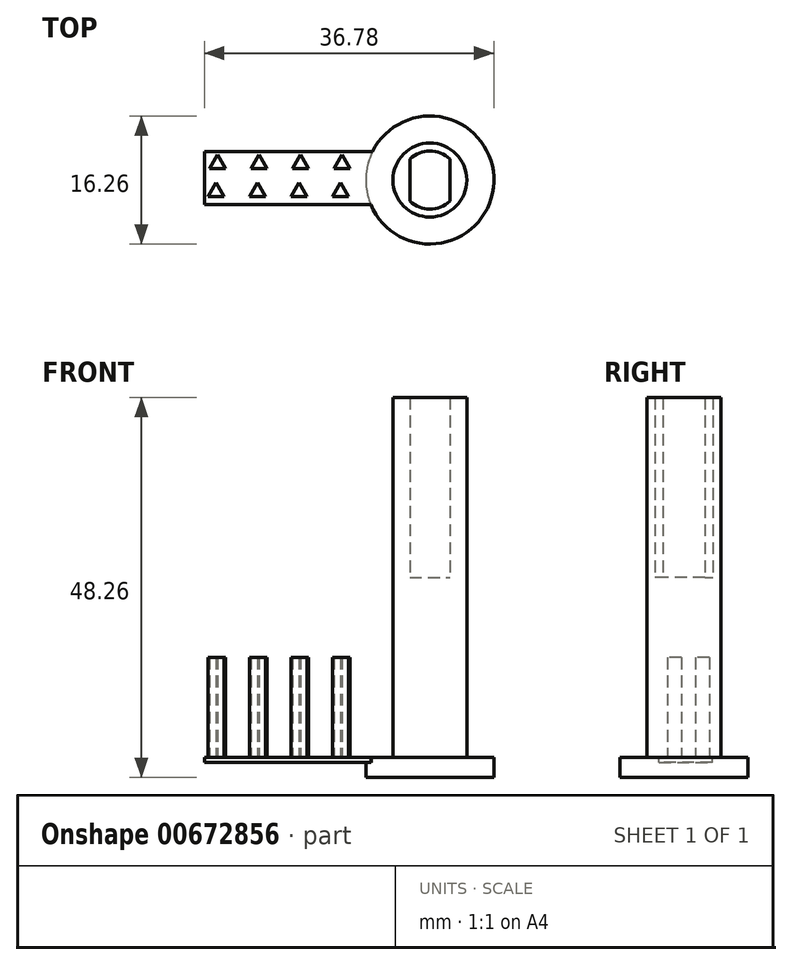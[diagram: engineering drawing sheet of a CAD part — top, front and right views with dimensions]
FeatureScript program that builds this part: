
annotation { "Feature Type Name" : "Feature", "Feature Type Description" : "" }
export const myFeature = defineFeature(function(context is Context, id is Id, definition is map)
    precondition{}
    {
        {
            var Q0;
            Q0=qCreatedBy(makeId("Top.planeOp"),FACE);
            var sketch = newSketch(context, id + "F0", { "sketchPlane" : qUnion([Q0])});
            skCircle(sketch, "E0", {"center": v(0, 0) * mm, "radius": 4.7 * mm});
            skCircle(sketch, "E1", {"center": v(0, 0) * mm, "radius": 3.68 * mm});
            skLineSegment(sketch, "E2", {"start": v(0, 0) * mm, "end": v(-2.54, 0) * mm});
            skLineSegment(sketch, "E3", {"start": v(0, 0) * mm, "end": v(2.54, 0) * mm});
            skLineSegment(sketch, "E4.bottom", {"start": v(2.54, 2.67) * mm, "end": v(3.77, 2.67) * mm});
            skLineSegment(sketch, "E4.top", {"start": v(2.54, -2.8) * mm, "end": v(3.77, -2.8) * mm});
            skLineSegment(sketch, "E4.left", {"start": v(2.54, 2.67) * mm, "end": v(2.54, -2.8) * mm});
            skLineSegment(sketch, "E4.right", {"start": v(3.77, 2.67) * mm, "end": v(3.77, -2.8) * mm});
            skLineSegment(sketch, "E5.bottom", {"start": v(-2.54, 2.67) * mm, "end": v(-3.77, 2.67) * mm});
            skLineSegment(sketch, "E5.top", {"start": v(-2.54, -2.8) * mm, "end": v(-3.77, -2.8) * mm});
            skLineSegment(sketch, "E5.left", {"start": v(-2.54, 2.67) * mm, "end": v(-2.54, -2.8) * mm});
            skLineSegment(sketch, "E5.right", {"start": v(-3.77, 2.67) * mm, "end": v(-3.77, -2.8) * mm});
            skSolve(sketch);
        }
        {
            var Q0;
            {var subQ1=sQuery(id+"F0.wireOp",EDGE,"E4.top");Q0=makeQuery(id+"F0.imprint","IMPRINT",FACE,{"disambiguationData":[TD([[makeQuery(id+"F0.imprint","IMPRINT",EDGE,{"derivedFrom":subQ1}),-1.0]])]});}
            var Q1;
            {var subQ0=sQuery(id+"F0.wireOp",EDGE,"E4.left");var subQ4=makeQuery(id+"F0.imprint","INTERSECT",VERTEX,{"derivedFrom":[sQuery(id+"F0.wireOp",EDGE,"E3"),subQ0]});Q1=makeQuery(id+"F0.imprint","IMPRINT",FACE,{"disambiguationData":[TD([[makeQuery(id+"F0.imprint","IMPRINT",EDGE,{"disambiguationData":[TD([[subQ4,-1.0]])],"derivedFrom":subQ0}),1.0]])]});}
            var Q2;
            {var subQ4=sQuery(id+"F0.wireOp",EDGE,"E4.bottom");Q2=makeQuery(id+"F0.imprint","IMPRINT",FACE,{"disambiguationData":[TD([[makeQuery(id+"F0.imprint","IMPRINT",EDGE,{"derivedFrom":subQ4}),-1.0]])]});}
            var Q3;
            {var subQ1=sQuery(id+"F0.wireOp",EDGE,"E4.bottom");Q3=makeQuery(id+"F0.imprint","IMPRINT",FACE,{"disambiguationData":[TD([[makeQuery(id+"F0.imprint","IMPRINT",EDGE,{"derivedFrom":subQ1}),1.0]])]});}
            var Q4;
            {var subQ1=sQuery(id+"F0.wireOp",EDGE,"E5.bottom");Q4=makeQuery(id+"F0.imprint","IMPRINT",FACE,{"disambiguationData":[TD([[makeQuery(id+"F0.imprint","IMPRINT",EDGE,{"derivedFrom":subQ1}),1.0]])]});}
            var Q5;
            {var subQ0=sQuery(id+"F0.wireOp",EDGE,"E5.left");var subQ4=makeQuery(id+"F0.imprint","INTERSECT",VERTEX,{"derivedFrom":[sQuery(id+"F0.wireOp",EDGE,"E2"),subQ0]});Q5=makeQuery(id+"F0.imprint","IMPRINT",FACE,{"disambiguationData":[TD([[makeQuery(id+"F0.imprint","IMPRINT",EDGE,{"disambiguationData":[TD([[subQ4,-1.0]])],"derivedFrom":subQ0}),-1.0]])]});}
            extrude(context, id + "F1", {"entities" : qUnion([Q0, Q1, Q2, Q3, Q4, Q5]), "depth" : 48.26 * mm, "offsetDistance" : 25.4 * mm});
        }
        {
            var Q0;
            {var subQ4=sQuery(id+"F0.wireOp",EDGE,"E2");Q0=makeQuery(id+"F0.imprint","IMPRINT",FACE,{"disambiguationData":[TD([[makeQuery(id+"F0.imprint","IMPRINT",EDGE,{"derivedFrom":subQ4}),1.0]])]});}
            var Q1;
            {var subQ4=sQuery(id+"F0.wireOp",EDGE,"E2");Q1=makeQuery(id+"F0.imprint","IMPRINT",FACE,{"disambiguationData":[TD([[makeQuery(id+"F0.imprint","IMPRINT",EDGE,{"derivedFrom":subQ4}),-1.0]])]});}
            extrude(context, id + "F2", {"entities" : qUnion([Q0, Q1]), "operationType" : NewBodyOperationType.ADD, "depth" : 25.4 * mm, "offsetDistance" : 25.4 * mm});
        }
        {
            var Q0;
            Q0=qCreatedBy(makeId("Top.planeOp"),FACE);
            var sketch = newSketch(context, id + "F3", { "sketchPlane" : qUnion([Q0])});
            skCircle(sketch, "E6", {"center": v(0, 0) * mm, "radius": 8.13 * mm});
            skSolve(sketch);
        }
        {
            var Q0;
            Q0 = qSketchRegion(id + "F3", true);
            extrude(context, id + "F4", {"entities" : qUnion([Q0]), "operationType" : NewBodyOperationType.ADD, "depth" : 2.54 * mm, "offsetDistance" : 25.4 * mm});
        }
        {
            var Q0;
            Q0=makeQuery(id+"F4.opExtrude","CAP_FACE",FACE,{"disambiguationData":[OSD([sQuery(id+"F3.wireOp",EDGE,"E6")])],"isStart":false});
            var sketch = newSketch(context, id + "F5", { "sketchPlane" : qUnion([Q0])});
            skLineSegment(sketch, "E7.bottom", {"start": v(-3.25, -3.13) * mm, "end": v(-28.65, -3.13) * mm});
            skLineSegment(sketch, "E7.top", {"start": v(-3.25, 3.6) * mm, "end": v(-28.65, 3.6) * mm});
            skLineSegment(sketch, "E7.left", {"start": v(-3.25, -3.13) * mm, "end": v(-3.25, 3.6) * mm});
            skLineSegment(sketch, "E7.right", {"start": v(-28.65, -3.13) * mm, "end": v(-28.65, 3.6) * mm});
            skSolve(sketch);
        }
        {
            var Q0;
            {var subQ0=sQuery(id+"F5.wireOp",EDGE,"E7.right");Q0=makeQuery(id+"F5.imprint","IMPRINT",FACE,{"disambiguationData":[TD([[makeQuery(id+"F5.imprint","IMPRINT",EDGE,{"derivedFrom":subQ0}),-1.0]])]});}
            extrude(context, id + "F6", {"entities" : qUnion([Q0]), "operationType" : NewBodyOperationType.ADD, "oppositeDirection" : true, "depth" : 0.64 * mm, "offsetDistance" : 25.4 * mm});
        }
        {
            var Q0;
            {var subQ0=sQuery(id+"F3.wireOp",EDGE,"E6");Q0=makeQuery(id+"F6.boolean.opBoolean","MERGE",FACE,{"derivedFrom":[makeQuery(id+"F4.opExtrude","CAP_FACE",FACE,{"disambiguationData":[OSD([subQ0])],"isStart":false}),makeQuery(id+"F6.opExtrude","CAP_FACE",FACE,{"disambiguationData":[OSD([subQ0,sQuery(id+"F5.wireOp",EDGE,"E7.bottom"),sQuery(id+"F5.wireOp",EDGE,"E7.top"),sQuery(id+"F5.wireOp",EDGE,"E7.right")])],"isStart":true})]});}
            var sketch = newSketch(context, id + "F7", { "sketchPlane" : qUnion([Q0])});
            skLineSegment(sketch, "E8", {"start": v(-28.02, 1.48) * mm, "end": v(-25.99, 1.48) * mm});
            skLineSegment(sketch, "E9", {"start": v(-25.99, 1.48) * mm, "end": v(-27, 3.24) * mm});
            skLineSegment(sketch, "E10", {"start": v(-27, 3.24) * mm, "end": v(-28.02, 1.48) * mm});
            skLineSegment(sketch, "E11.1.0.0", {"start": v(-20.7, 1.48) * mm, "end": v(-21.72, 3.24) * mm});
            skLineSegment(sketch, "E11.1.0.1", {"start": v(-21.72, 3.24) * mm, "end": v(-22.73, 1.48) * mm});
            skLineSegment(sketch, "E11.1.0.2", {"start": v(-22.73, 1.48) * mm, "end": v(-20.7, 1.48) * mm});
            skLineSegment(sketch, "E11.2.0.0", {"start": v(-15.42, 1.48) * mm, "end": v(-16.43, 3.24) * mm});
            skLineSegment(sketch, "E11.2.0.1", {"start": v(-16.43, 3.24) * mm, "end": v(-17.45, 1.48) * mm});
            skLineSegment(sketch, "E11.2.0.2", {"start": v(-17.45, 1.48) * mm, "end": v(-15.42, 1.48) * mm});
            skLineSegment(sketch, "E11.3.0.0", {"start": v(-10.14, 1.48) * mm, "end": v(-11.15, 3.24) * mm});
            skLineSegment(sketch, "E11.3.0.1", {"start": v(-11.15, 3.24) * mm, "end": v(-12.17, 1.48) * mm});
            skLineSegment(sketch, "E11.3.0.2", {"start": v(-12.17, 1.48) * mm, "end": v(-10.14, 1.48) * mm});
            skLineSegment(sketch, "E11.direction1", {"start": v(-28.02, 1.48) * mm, "end": v(-22.73, 1.48) * mm, "construction": true});
            skLineSegment(sketch, "E12", {"start": v(-28.2, -2.09) * mm, "end": v(-26.16, -2.09) * mm});
            skLineSegment(sketch, "E13", {"start": v(-26.16, -2.09) * mm, "end": v(-27.17, -0.33) * mm});
            skLineSegment(sketch, "E14", {"start": v(-27.17, -0.33) * mm, "end": v(-28.2, -2.09) * mm});
            skLineSegment(sketch, "E15.1.0.0", {"start": v(-20.87, -2.09) * mm, "end": v(-21.9, -0.33) * mm});
            skLineSegment(sketch, "E15.1.0.1", {"start": v(-21.9, -0.33) * mm, "end": v(-22.9, -2.09) * mm});
            skLineSegment(sketch, "E15.1.0.2", {"start": v(-22.9, -2.09) * mm, "end": v(-20.87, -2.09) * mm});
            skLineSegment(sketch, "E15.2.0.0", {"start": v(-15.6, -2.09) * mm, "end": v(-16.6, -0.33) * mm});
            skLineSegment(sketch, "E15.2.0.1", {"start": v(-16.6, -0.33) * mm, "end": v(-17.62, -2.09) * mm});
            skLineSegment(sketch, "E15.2.0.2", {"start": v(-17.62, -2.09) * mm, "end": v(-15.6, -2.09) * mm});
            skLineSegment(sketch, "E15.3.0.0", {"start": v(-10.3, -2.09) * mm, "end": v(-11.32, -0.33) * mm});
            skLineSegment(sketch, "E15.3.0.1", {"start": v(-11.32, -0.33) * mm, "end": v(-12.34, -2.09) * mm});
            skLineSegment(sketch, "E15.3.0.2", {"start": v(-12.34, -2.09) * mm, "end": v(-10.3, -2.09) * mm});
            skLineSegment(sketch, "E15.direction1", {"start": v(-28.2, -2.09) * mm, "end": v(-22.9, -2.09) * mm, "construction": true});
            skSolve(sketch);
        }
        {
            var Q0;
            Q0 = qSketchRegion(id + "F7", true);
            extrude(context, id + "F8", {"entities" : qUnion([Q0]), "operationType" : NewBodyOperationType.ADD, "depth" : 12.7 * mm, "offsetDistance" : 25.4 * mm});
        }
    });
